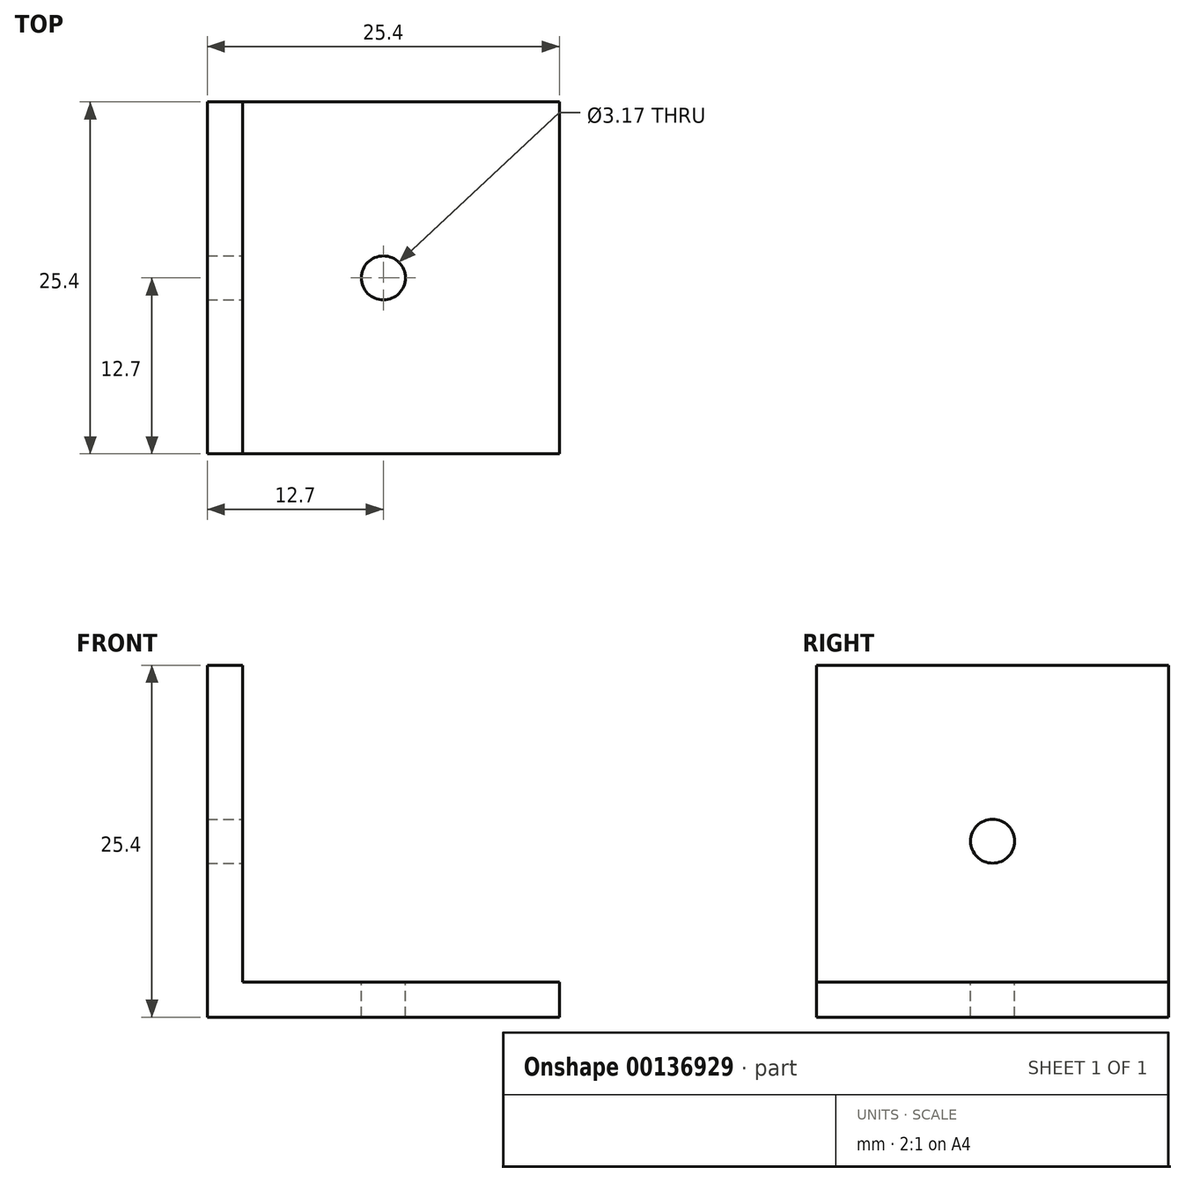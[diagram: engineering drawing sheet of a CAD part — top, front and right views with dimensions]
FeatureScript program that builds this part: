
annotation { "Feature Type Name" : "Feature", "Feature Type Description" : "" }
export const myFeature = defineFeature(function(context is Context, id is Id, definition is map)
    precondition{}
    {
        {
            var Q0;
            Q0=qCreatedBy(makeId("Front.planeOp"),FACE);
            var sketch = newSketch(context, id + "F0", { "sketchPlane" : qUnion([Q0])});
            skLineSegment(sketch, "E0", {"start": v(0, 0) * mm, "end": v(0, 25.4) * mm});
            skLineSegment(sketch, "E1", {"start": v(0, 25.4) * mm, "end": v(2.54, 25.4) * mm});
            skLineSegment(sketch, "E2", {"start": v(0, 0) * mm, "end": v(25.4, 0) * mm});
            skLineSegment(sketch, "E3", {"start": v(25.4, 0) * mm, "end": v(25.4, 2.54) * mm});
            skLineSegment(sketch, "E4", {"start": v(25.4, 2.54) * mm, "end": v(2.54, 2.54) * mm});
            skLineSegment(sketch, "E5", {"start": v(2.54, 25.4) * mm, "end": v(2.54, 2.54) * mm});
            skSolve(sketch);
        }
        {
            var Q0;
            Q0=makeQuery(id+"F0.imprint","IMPRINT",FACE,{"disambiguationData":[TD([[makeQuery(id+"F0.imprint","IMPRINT",EDGE,{"derivedFrom":sQuery(id+"F0.wireOp",EDGE,"E0")}),-1.0]])]});
            extrude(context, id + "F1", {"entities" : qUnion([Q0]), "depth" : 25.4 * mm});
        }
        {
            var Q0;
            Q0=makeQuery(id+"F1.opExtrude","SWEPT_FACE",FACE,{"disambiguationData":[OSD([sQuery(id+"F0.wireOp",EDGE,"E5")])]});
            var sketch = newSketch(context, id + "F2", { "sketchPlane" : qUnion([Q0])});
            skLineSegment(sketch, "E6.bottom", {"start": v(-25.4, 25.4) * mm, "end": v(0, 25.4) * mm});
            skLineSegment(sketch, "E6.top", {"start": v(-25.4, 2.54) * mm, "end": v(0, 2.54) * mm});
            skLineSegment(sketch, "E6.left", {"start": v(-25.4, 25.4) * mm, "end": v(-25.4, 2.54) * mm});
            skLineSegment(sketch, "E6.right", {"start": v(0, 25.4) * mm, "end": v(0, 2.54) * mm});
            skLineSegment(sketch, "E7", {"start": v(-12.7, 25.4) * mm, "end": v(-12.7, 12.7) * mm});
            skPoint(sketch, "E8", {"position": v(-12.7, 12.7) * mm});
            skSolve(sketch);
        }
        {
            var Q0;
            Q0=makeQuery(id+"F1.opExtrude","SWEPT_FACE",FACE,{"disambiguationData":[OSD([sQuery(id+"F0.wireOp",EDGE,"E4")])]});
            var sketch = newSketch(context, id + "F3", { "sketchPlane" : qUnion([Q0])});
            skLineSegment(sketch, "E9.bottom", {"start": v(2.54, 0) * mm, "end": v(25.4, 0) * mm});
            skLineSegment(sketch, "E9.top", {"start": v(2.54, -25.4) * mm, "end": v(25.4, -25.4) * mm});
            skLineSegment(sketch, "E9.left", {"start": v(2.54, 0) * mm, "end": v(2.54, -25.4) * mm});
            skLineSegment(sketch, "E9.right", {"start": v(25.4, 0) * mm, "end": v(25.4, -25.4) * mm});
            skLineSegment(sketch, "E10", {"start": v(25.4, -12.7) * mm, "end": v(12.7, -12.7) * mm});
            skPoint(sketch, "E11", {"position": v(12.7, -12.7) * mm});
            skSolve(sketch);
        }
        {
            var Q0;
            Q0=sQuery(id+"F2.wireOp",VERTEX,"E8");
            var Q1;
            Q1=sQuery(id+"F3.wireOp",VERTEX,"E11");
            var Q2;
            Q2=makeQuery(id+"F1.opExtrude","SWEPT_BODY",BODY,{"disambiguationData":[OSD([sQuery(id+"F0.wireOp",EDGE,"E0"),sQuery(id+"F0.wireOp",EDGE,"E1"),sQuery(id+"F0.wireOp",EDGE,"E2"),sQuery(id+"F0.wireOp",EDGE,"E3"),sQuery(id+"F0.wireOp",EDGE,"E4"),sQuery(id+"F0.wireOp",EDGE,"E5")])]});
            hole(context, id + "F4", {"style" : HoleStyle.SIMPLE, "endStyle" : HoleEndStyle.THROUGH, "holeDiameter" : 3.17 * mm, "locations" : qUnion([Q0, Q1]), "scope" : qUnion([Q2]), "isTappedThrough" : true});
        }
    });
